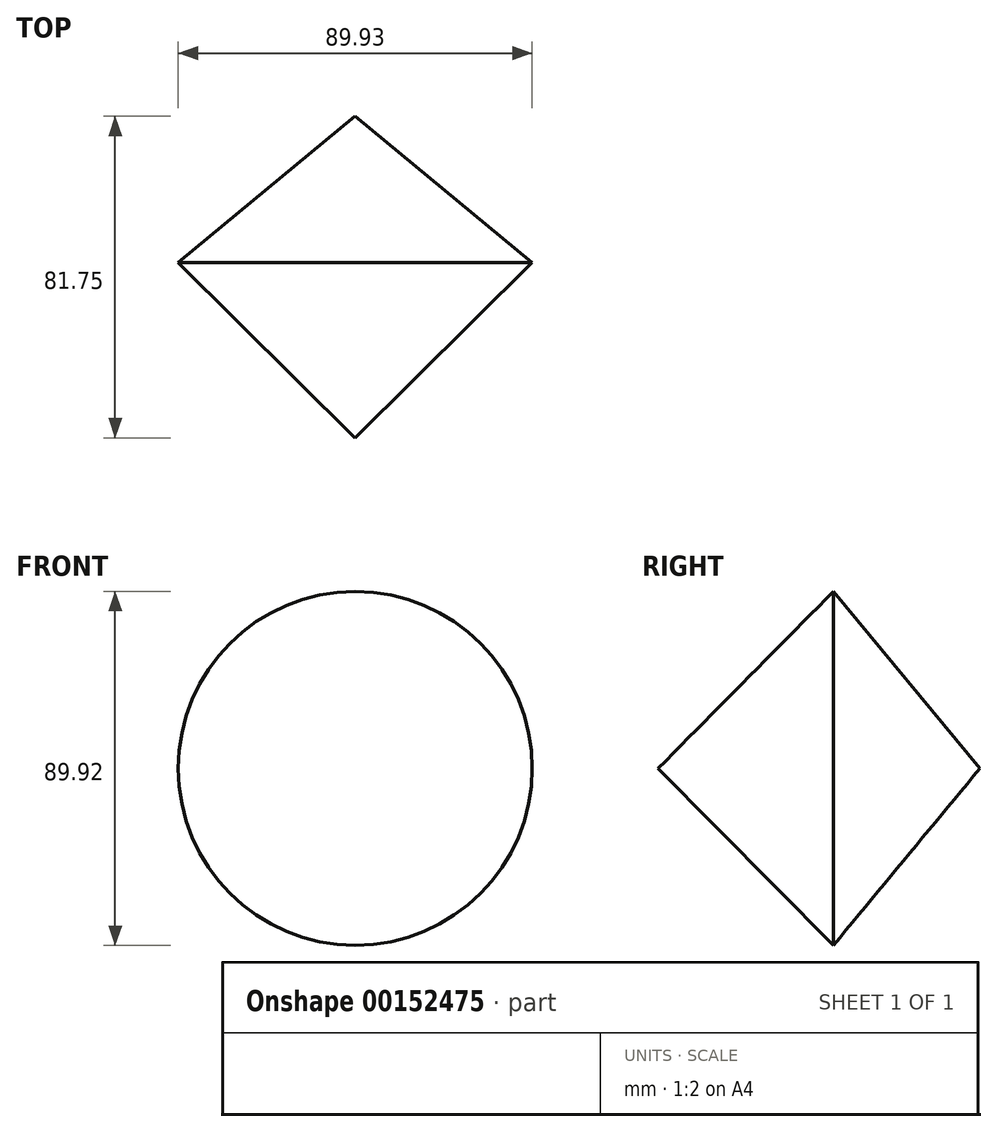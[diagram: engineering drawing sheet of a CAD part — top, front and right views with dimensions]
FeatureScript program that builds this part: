
annotation { "Feature Type Name" : "Feature", "Feature Type Description" : "" }
export const myFeature = defineFeature(function(context is Context, id is Id, definition is map)
    precondition{}
    {
        {
            var Q0;
            Q0=qCreatedBy(makeId("Top.planeOp"),FACE);
            var sketch = newSketch(context, id + "F0", { "sketchPlane" : qUnion([Q0])});
            skLineSegment(sketch, "E0", {"start": v(-25.7, 37.23) * mm, "end": v(-25.7, -44.52) * mm});
            skLineSegment(sketch, "E1", {"start": v(-25.7, -44.52) * mm, "end": v(-70.66, 0) * mm});
            skLineSegment(sketch, "E2", {"start": v(-70.66, 0) * mm, "end": v(-25.7, 37.23) * mm});
            skSolve(sketch);
        }
        {
            var Q0;
            Q0=makeQuery(id+"F0.imprint","IMPRINT",FACE,{"disambiguationData":[TD([[makeQuery(id+"F0.imprint","IMPRINT",EDGE,{"derivedFrom":sQuery(id+"F0.wireOp",EDGE,"E0")}),-1.0]])]});
            var Q1;
            Q1=sQuery(id+"F0.wireOp",EDGE,"E0");
            revolve(context, id + "F1", {"entities" : qUnion([Q0]), "axis" : qUnion([Q1]), "revolveType" : RevolveType.FULL});
        }
    });
